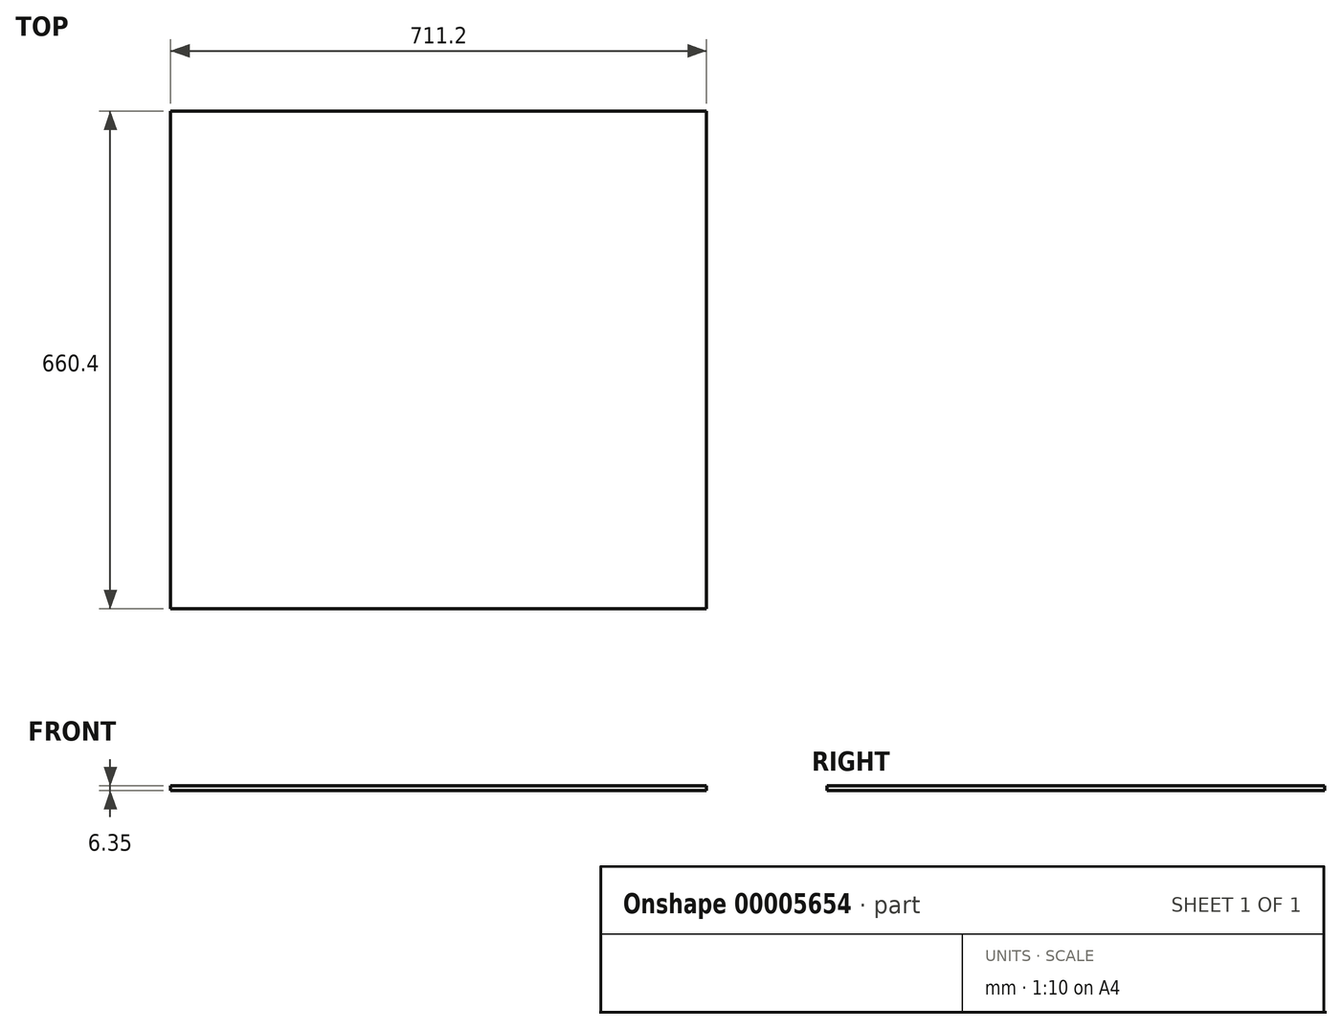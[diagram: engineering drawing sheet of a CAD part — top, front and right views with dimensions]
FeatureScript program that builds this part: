
annotation { "Feature Type Name" : "Feature", "Feature Type Description" : "" }
export const myFeature = defineFeature(function(context is Context, id is Id, definition is map)
    precondition{}
    {
        {
            var Q0;
            Q0=qCreatedBy(makeId("Top.planeOp"),FACE);
            var sketch = newSketch(context, id + "F0", { "sketchPlane" : qUnion([Q0])});
            skLineSegment(sketch, "E0.bottom", {"start": v(0, 660.4) * mm, "end": v(711.2, 660.4) * mm});
            skLineSegment(sketch, "E0.top", {"start": v(0, 0) * mm, "end": v(711.2, 0) * mm});
            skLineSegment(sketch, "E0.left", {"start": v(0, 660.4) * mm, "end": v(0, 0) * mm});
            skLineSegment(sketch, "E0.right", {"start": v(711.2, 660.4) * mm, "end": v(711.2, 0) * mm});
            skSolve(sketch);
        }
        {
            var Q0;
            Q0=makeQuery(id+"F0.imprint","IMPRINT",FACE,{"disambiguationData":[TD([[makeQuery(id+"F0.imprint","IMPRINT",EDGE,{"derivedFrom":sQuery(id+"F0.wireOp",EDGE,"E0.bottom")}),-1.0]])]});
            extrude(context, id + "F1", {"entities" : qUnion([Q0]), "depth" : 6.35 * mm});
        }
    });
